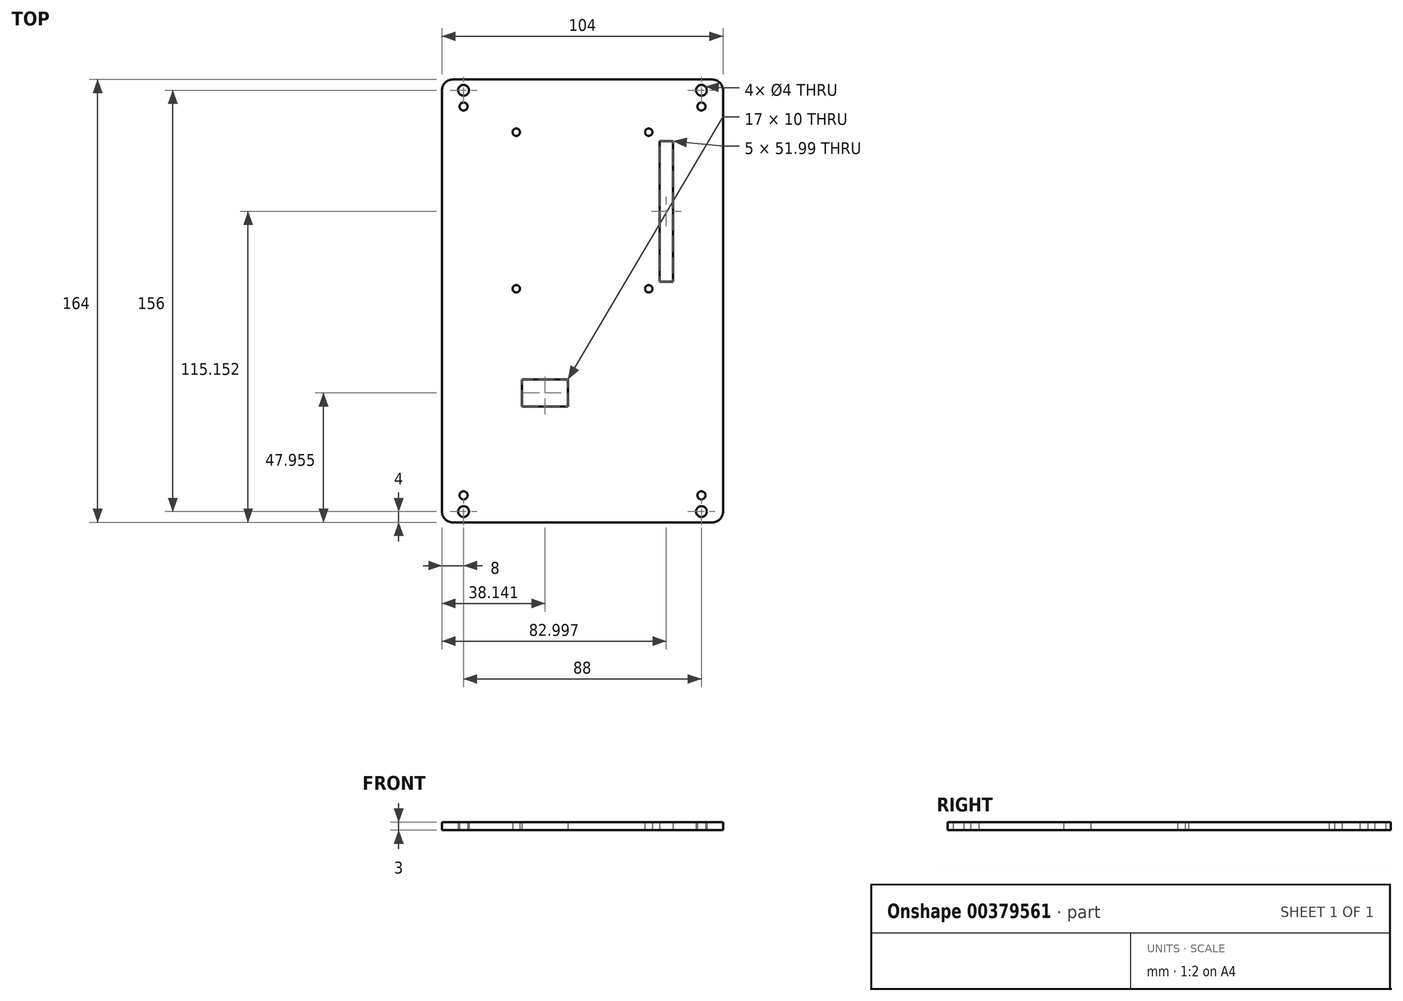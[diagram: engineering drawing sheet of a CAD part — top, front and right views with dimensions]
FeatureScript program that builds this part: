
annotation { "Feature Type Name" : "Feature", "Feature Type Description" : "" }
export const myFeature = defineFeature(function(context is Context, id is Id, definition is map)
    precondition{}
    {
        {
            var Q0;
            Q0=qCreatedBy(makeId("Top.planeOp"),FACE);
            var sketch = newSketch(context, id + "F0", { "sketchPlane" : qUnion([Q0])});
            skLineSegment(sketch, "E0.bottom", {"start": v(48, -82) * mm, "end": v(-48, -82) * mm});
            skLineSegment(sketch, "E0.top", {"start": v(48, 82) * mm, "end": v(-48, 82) * mm});
            skLineSegment(sketch, "E0.left", {"start": v(52, -78) * mm, "end": v(52, 78) * mm});
            skLineSegment(sketch, "E0.right", {"start": v(-52, -78) * mm, "end": v(-52, 78) * mm});
            skPoint(sketch, "E0.middle", {"position": v(0, 0) * mm});
            skLineSegment(sketch, "E1", {"start": v(-55.89, 78) * mm, "end": v(56.98, 78) * mm, "construction": true});
            skLineSegment(sketch, "E2", {"start": v(-48, 86.7) * mm, "end": v(-48, -87.9) * mm, "construction": true});
            skLineSegment(sketch, "E3", {"start": v(0, 97.18) * mm, "end": v(0, -103.74) * mm, "construction": true});
            skPoint(sketch, "E3.endSnap0", {"position": v(0, -82) * mm});
            skPoint(sketch, "E4.endSnap0", {"position": v(-48, -0.6) * mm});
            skLineSegment(sketch, "E5", {"start": v(-56.62, 0) * mm, "end": v(57, 0) * mm, "construction": true});
            skLineSegment(sketch, "E6.MirrorCS", {"start": v(48, 86.7) * mm, "end": v(48, -87.9) * mm, "construction": true});
            skLineSegment(sketch, "E7.MirrorCS", {"start": v(-55.89, -78) * mm, "end": v(56.98, -78) * mm, "construction": true});
            skCircle(sketch, "E8", {"center": v(-44, 78) * mm, "radius": 2 * mm});
            skCircle(sketch, "E9.MirrorC", {"center": v(-24.5, 62.49) * mm, "radius": 1.37 * mm});
            skCircle(sketch, "E10.MirrorC", {"center": v(24.5, 4.5) * mm, "radius": 1.37 * mm});
            skCircle(sketch, "E11.MirrorC", {"center": v(24.5, 62.49) * mm, "radius": 1.37 * mm});
            skCircle(sketch, "E12.MirrorC", {"center": v(-24.5, 4.5) * mm, "radius": 1.37 * mm});
            skPoint(sketch, "E13.visualSharp", {"position": v(-52, 82) * mm});
            skArc(sketch, "E13.filletArc", {"start": v(-48, 82) * mm, "mid": v(-50.83, 80.83) * mm, "end": v(-52, 78) * mm});
            skPoint(sketch, "E14.visualSharp", {"position": v(52, 82) * mm});
            skArc(sketch, "E14.filletArc", {"start": v(52, 78) * mm, "mid": v(50.83, 80.83) * mm, "end": v(48, 82) * mm});
            skPoint(sketch, "E15.visualSharp", {"position": v(52, -82) * mm});
            skArc(sketch, "E15.filletArc", {"start": v(48, -82) * mm, "mid": v(50.83, -80.83) * mm, "end": v(52, -78) * mm});
            skPoint(sketch, "E16.visualSharp", {"position": v(-52, -82) * mm});
            skArc(sketch, "E16.filletArc", {"start": v(-52, -78) * mm, "mid": v(-50.83, -80.83) * mm, "end": v(-48, -82) * mm});
            skLineSegment(sketch, "E17.bottom", {"start": v(28.5, 59.15) * mm, "end": v(33.5, 59.15) * mm});
            skLineSegment(sketch, "E17.top", {"start": v(28.5, 7.16) * mm, "end": v(33.5, 7.16) * mm});
            skLineSegment(sketch, "E17.left", {"start": v(28.5, 59.15) * mm, "end": v(28.5, 7.16) * mm});
            skLineSegment(sketch, "E17.right", {"start": v(33.5, 59.15) * mm, "end": v(33.5, 7.16) * mm});
            skLineSegment(sketch, "E18", {"start": v(28.5, 84.78) * mm, "end": v(28.5, -4.96) * mm, "construction": true});
            skLineSegment(sketch, "E19", {"start": v(-54.96, 58.49) * mm, "end": v(56.01, 58.49) * mm, "construction": true});
            skLineSegment(sketch, "E20", {"start": v(20.58, 33.15) * mm, "end": v(39.47, 33.15) * mm, "construction": true});
            skPoint(sketch, "E20.startSnap0", {"position": v(28.5, 33.15) * mm});
            skLineSegment(sketch, "E21", {"start": v(-56.62, -29.05) * mm, "end": v(57, -29.05) * mm, "construction": true});
            skLineSegment(sketch, "E22.bottom", {"start": v(-22.36, -29.05) * mm, "end": v(-5.36, -29.05) * mm});
            skLineSegment(sketch, "E22.top", {"start": v(-22.36, -39.05) * mm, "end": v(-5.36, -39.05) * mm});
            skLineSegment(sketch, "E22.left", {"start": v(-22.36, -29.05) * mm, "end": v(-22.36, -39.05) * mm});
            skLineSegment(sketch, "E23", {"start": v(-5.36, -29.05) * mm, "end": v(-5.36, -39.05) * mm});
            skLineSegment(sketch, "E24", {"start": v(-44, 86.75) * mm, "end": v(-44, -88.25) * mm, "construction": true});
            skLineSegment(sketch, "E25.MirrorCS", {"start": v(44, 86.75) * mm, "end": v(44, -88.25) * mm, "construction": true});
            skCircle(sketch, "E26.MirrorC", {"center": v(44, 78) * mm, "radius": 2 * mm});
            skCircle(sketch, "E27.MirrorC", {"center": v(-44, -78) * mm, "radius": 2 * mm});
            skCircle(sketch, "E28.MirrorC", {"center": v(44, -78) * mm, "radius": 2 * mm});
            skLineSegment(sketch, "E29", {"start": v(-54.83, 72) * mm, "end": v(56.5, 72) * mm, "construction": true});
            skLineSegment(sketch, "E30.MirrorCS", {"start": v(-54.83, -72) * mm, "end": v(56.5, -72) * mm, "construction": true});
            skCircle(sketch, "E31", {"center": v(-44, 72) * mm, "radius": 1.5 * mm});
            skCircle(sketch, "E32.MirrorC", {"center": v(44, 72) * mm, "radius": 1.5 * mm});
            skCircle(sketch, "E33.MirrorC", {"center": v(-44, -72) * mm, "radius": 1.5 * mm});
            skCircle(sketch, "E34.MirrorC", {"center": v(44, -72) * mm, "radius": 1.5 * mm});
            skSolve(sketch);
        }
        {
            var Q0;
            Q0 = qSketchRegion(id + "F0", true);
            extrude(context, id + "F1", {"entities" : qUnion([Q0]), "depth" : 3 * mm});
        }
    });
